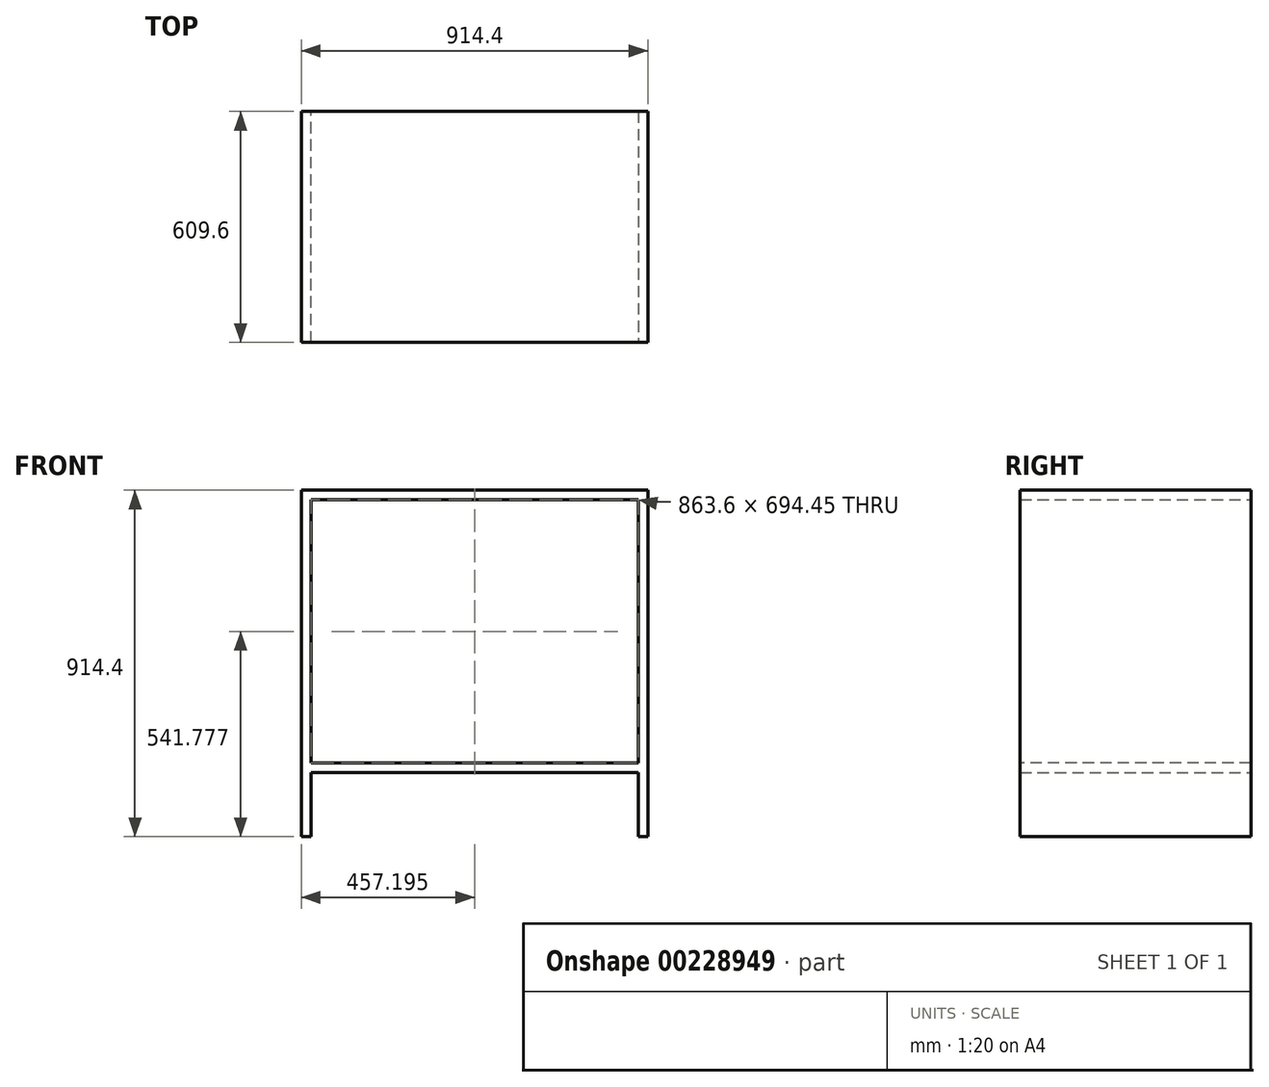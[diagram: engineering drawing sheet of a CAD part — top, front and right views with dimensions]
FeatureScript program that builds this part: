
annotation { "Feature Type Name" : "Feature", "Feature Type Description" : "" }
export const myFeature = defineFeature(function(context is Context, id is Id, definition is map)
    precondition{}
    {
        {
            var Q0;
            Q0=qCreatedBy(makeId("Top.planeOp"),FACE);
            var sketch = newSketch(context, id + "F0", { "sketchPlane" : qUnion([Q0])});
            skLineSegment(sketch, "E0.bottom", {"start": v(-458.35, -300.23) * mm, "end": v(456.05, -300.23) * mm});
            skLineSegment(sketch, "E0.top", {"start": v(-458.35, 309.37) * mm, "end": v(456.05, 309.37) * mm});
            skLineSegment(sketch, "E0.left", {"start": v(-458.35, -300.23) * mm, "end": v(-458.35, 309.37) * mm});
            skLineSegment(sketch, "E0.right", {"start": v(456.05, -300.23) * mm, "end": v(456.05, 309.37) * mm});
            skSolve(sketch);
        }
        {
            var Q0;
            Q0=makeQuery(id+"F0.imprint","IMPRINT",FACE,{"disambiguationData":[TD([[makeQuery(id+"F0.imprint","IMPRINT",EDGE,{"derivedFrom":sQuery(id+"F0.wireOp",EDGE,"E0.bottom")}),1.0]])]});
            extrude(context, id + "F1", {"entities" : qUnion([Q0]), "depth" : 914.4 * mm});
        }
        {
            var Q0;
            Q0=makeQuery(id+"F1.opExtrude","CAP_FACE",FACE,{"disambiguationData":[OSD([sQuery(id+"F0.wireOp",EDGE,"E0.bottom"),sQuery(id+"F0.wireOp",EDGE,"E0.top"),sQuery(id+"F0.wireOp",EDGE,"E0.left"),sQuery(id+"F0.wireOp",EDGE,"E0.right")])],"isStart":true});
            var Q1;
            Q1=makeQuery(id+"F1.opExtrude","SWEPT_FACE",FACE,{"disambiguationData":[OSD([sQuery(id+"F0.wireOp",EDGE,"E0.bottom")])]});
            var Q2;
            Q2=makeQuery(id+"F1.opExtrude","SWEPT_FACE",FACE,{"disambiguationData":[OSD([sQuery(id+"F0.wireOp",EDGE,"E0.top")])]});
            shell(context, id + "F2", {"entities" : qUnion([Q0, Q1, Q2]), "thickness" : 25.4 * mm});
        }
        {
            var Q0;
            Q0=makeQuery(id+"F2.opShell","OFFSET_FACE",FACE,{"disambiguationData":[OSD([sQuery(id+"F0.wireOp",EDGE,"E0.left")])]});
            var sketch = newSketch(context, id + "F3", { "sketchPlane" : qUnion([Q0])});
            skLineSegment(sketch, "E1.bottom", {"start": v(-300.23, 169.15) * mm, "end": v(309.37, 169.15) * mm});
            skLineSegment(sketch, "E1.top", {"start": v(-300.23, 194.55) * mm, "end": v(309.37, 194.55) * mm});
            skLineSegment(sketch, "E1.left", {"start": v(-300.23, 169.15) * mm, "end": v(-300.23, 194.55) * mm});
            skLineSegment(sketch, "E1.right", {"start": v(309.37, 169.15) * mm, "end": v(309.37, 194.55) * mm});
            skSolve(sketch);
        }
        {
            var Q0;
            Q0=qSketchRegion(id+"F3",true);
            extrude(context, id + "F4", {"entities" : qUnion([Q0]), "operationType" : NewBodyOperationType.ADD, "endBound" : BoundingType.UP_TO_NEXT, "depth" : 25.4 * mm});
        }
    });
